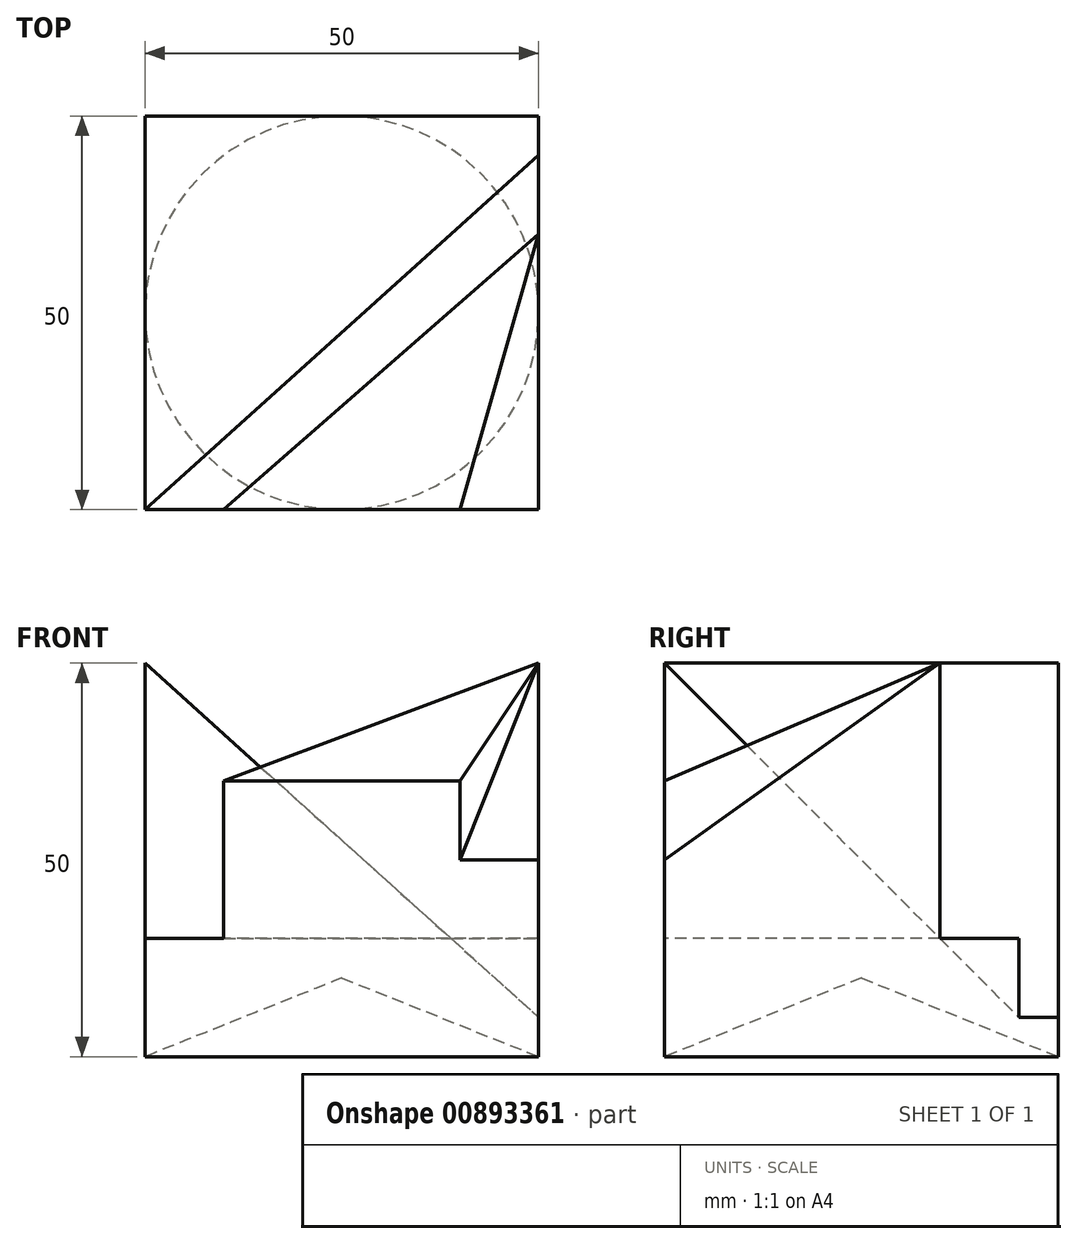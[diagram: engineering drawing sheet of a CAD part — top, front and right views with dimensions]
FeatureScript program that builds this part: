
annotation { "Feature Type Name" : "Feature", "Feature Type Description" : "" }
export const myFeature = defineFeature(function(context is Context, id is Id, definition is map)
    precondition{}
    {
        {
            var Q0;
            Q0=qCreatedBy(makeId("Top.planeOp"),FACE);
            var sketch = newSketch(context, id + "F0", { "sketchPlane" : qUnion([Q0])});
            skLineSegment(sketch, "E0.bottom", {"start": v(25, 25) * mm, "end": v(-25, 25) * mm});
            skLineSegment(sketch, "E0.top", {"start": v(25, -25) * mm, "end": v(-25, -25) * mm});
            skLineSegment(sketch, "E0.left", {"start": v(25, 25) * mm, "end": v(25, -25) * mm});
            skLineSegment(sketch, "E0.right", {"start": v(-25, 25) * mm, "end": v(-25, -25) * mm});
            skPoint(sketch, "E0.middle", {"position": v(0, 0) * mm});
            skSolve(sketch);
        }
        {
            var Q0;
            Q0=makeQuery(id+"F0.imprint","IMPRINT",FACE,{"disambiguationData":[TD([[makeQuery(id+"F0.imprint","IMPRINT",EDGE,{"derivedFrom":sQuery(id+"F0.wireOp",EDGE,"E0.bottom")}),1.0]])]});
            extrude(context, id + "F1", {"entities" : qUnion([Q0]), "depth" : 50 * mm, "offsetDistance" : 25 * mm});
        }
        {
            var Q0;
            Q0=makeQuery(id+"F1.opExtrude","CAP_FACE",FACE,{"disambiguationData":[OSD([sQuery(id+"F0.wireOp",EDGE,"E0.bottom"),sQuery(id+"F0.wireOp",EDGE,"E0.top"),sQuery(id+"F0.wireOp",EDGE,"E0.left"),sQuery(id+"F0.wireOp",EDGE,"E0.right")])],"isStart":true});
            cPlane(context, id + "F2", {"entities" : qUnion([Q0]), "cplaneType" : CPlaneType.OFFSET, "offset" : 15 * mm, "oppositeDirection" : true, "width" : 150 * mm, "height" : 150 * mm});
        }
        {
            var Q0;
            Q0=makeQuery(id+"F1.opExtrude","CAP_FACE",FACE,{"disambiguationData":[OSD([sQuery(id+"F0.wireOp",EDGE,"E0.bottom"),sQuery(id+"F0.wireOp",EDGE,"E0.top"),sQuery(id+"F0.wireOp",EDGE,"E0.left"),sQuery(id+"F0.wireOp",EDGE,"E0.right")])],"isStart":false});
            var sketch = newSketch(context, id + "F3", { "sketchPlane" : qUnion([Q0])});
            skLineSegment(sketch, "E1", {"start": v(-25, -25) * mm, "end": v(25, 20) * mm});
            skLineSegment(sketch, "E2", {"start": v(25, 20) * mm, "end": v(25, 10) * mm});
            skLineSegment(sketch, "E3", {"start": v(25, 10) * mm, "end": v(-15, -25) * mm});
            skLineSegment(sketch, "E4", {"start": v(-15, -25) * mm, "end": v(-25, -25) * mm});
            skSolve(sketch);
        }
        {
            var Q0;
            Q0=makeQuery(id+"F3.imprint","IMPRINT",FACE,{"disambiguationData":[TD([[makeQuery(id+"F3.imprint","IMPRINT",EDGE,{"derivedFrom":sQuery(id+"F3.wireOp",EDGE,"E1")}),-1.0]])]});
            var Q1;
            Q1=qCreatedBy(id+"F2.planeOp",FACE);
            extrude(context, id + "F4", {"entities" : qUnion([Q0]), "operationType" : NewBodyOperationType.REMOVE, "endBound" : BoundingType.UP_TO_SURFACE, "oppositeDirection" : true, "depth" : 25 * mm, "endBoundEntityFace" : qUnion([Q1]), "offsetDistance" : 25 * mm});
        }
        {
            var Q0;
            Q0=qCreatedBy(makeId("Front.planeOp"),FACE);
            var sketch = newSketch(context, id + "F5", { "sketchPlane" : qUnion([Q0])});
            skLineSegment(sketch, "E5", {"start": v(0, 0) * mm, "end": v(0, 10) * mm});
            skLineSegment(sketch, "E6", {"start": v(0, 10) * mm, "end": v(25, 0) * mm});
            skLineSegment(sketch, "E7", {"start": v(25, 0) * mm, "end": v(0, 0) * mm});
            skSolve(sketch);
        }
        {
            var Q0;
            Q0 = qSketchRegion(id + "F5", true);
            var Q1;
            Q1=sQuery(id+"F5.wireOp",EDGE,"E5");
            revolve(context, id + "F6", {"operationType" : NewBodyOperationType.REMOVE, "surfaceOperationType" : NewSurfaceOperationType.NEW, "entities" : qUnion([Q0]), "axis" : qUnion([Q1]), "revolveType" : RevolveType.FULL, "oppositeDirection" : true});
        }
        {
            var Q0;
            Q0=makeQuery(id+"F1.opExtrude","SWEPT_FACE",FACE,{"disambiguationData":[OSD([sQuery(id+"F0.wireOp",EDGE,"E0.top")])]});
            var sketch = newSketch(context, id + "F7", { "sketchPlane" : qUnion([Q0])});
            skLineSegment(sketch, "E8", {"start": v(-15, 50) * mm, "end": v(25, 50) * mm});
            skLineSegment(sketch, "E9", {"start": v(25, 50) * mm, "end": v(25, 25) * mm});
            skLineSegment(sketch, "E10", {"start": v(25, 25) * mm, "end": v(15, 25) * mm});
            skLineSegment(sketch, "E11", {"start": v(15, 25) * mm, "end": v(15, 35) * mm});
            skLineSegment(sketch, "E12", {"start": v(15, 35) * mm, "end": v(-15, 35) * mm});
            skLineSegment(sketch, "E13", {"start": v(-15, 35) * mm, "end": v(-15, 50) * mm});
            skSolve(sketch);
        }
        {
            var Q1;
            Q1=makeQuery(id+"F7.imprint","IMPRINT",FACE,{"disambiguationData":[TD([[makeQuery(id+"F7.imprint","IMPRINT",EDGE,{"derivedFrom":sQuery(id+"F7.wireOp",EDGE,"E8")}),1.0]])]});
            var Q2;
            Q2=makeQuery(id+"F4.boolean.opBoolean","COPY",VERTEX,{"derivedFrom":makeQuery(id+"F4.opExtrude","CAP_VERTEX",VERTEX,{"disambiguationData":[OSD([sQuery(id+"F0.wireOp",EDGE,"E0.left"),sQuery(id+"F3.wireOp",EDGE,"E2"),sQuery(id+"F3.wireOp",EDGE,"E3")])],"isStart":true})});
            loft(context, id + "F8", {"operationType" : NewBodyOperationType.REMOVE, "sheetProfilesArray" : [{ "sheetProfileEntities" : qUnion([Q1]) }, { "sheetProfileEntities" : qUnion([Q2]) }]});
        }
        {
            var Q0;
            Q0=makeQuery(id+"F1.opExtrude","SWEPT_FACE",FACE,{"disambiguationData":[OSD([sQuery(id+"F0.wireOp",EDGE,"E0.bottom")])]});
            var sketch = newSketch(context, id + "F9", { "sketchPlane" : qUnion([Q0])});
            skLineSegment(sketch, "E14", {"start": v(25, 50) * mm, "end": v(-25, 5) * mm});
            skLineSegment(sketch, "E15", {"start": v(-25, 5) * mm, "end": v(-25, 50) * mm});
            skLineSegment(sketch, "E16", {"start": v(-25, 50) * mm, "end": v(25, 50) * mm});
            skSolve(sketch);
        }
        {
            var Q0;
            Q0=makeQuery(id+"F9.imprint","IMPRINT",FACE,{"disambiguationData":[TD([[makeQuery(id+"F9.imprint","IMPRINT",EDGE,{"derivedFrom":sQuery(id+"F9.wireOp",EDGE,"E14")}),-1.0]])]});
            var Q1;
            Q1=makeQuery(id+"F4.boolean.opBoolean","COPY",FACE,{"derivedFrom":makeQuery(id+"F4.opExtrude","SWEPT_FACE",FACE,{"disambiguationData":[OSD([sQuery(id+"F3.wireOp",EDGE,"E1")])]})});
            extrude(context, id + "F10", {"entities" : qUnion([Q0]), "operationType" : NewBodyOperationType.REMOVE, "endBound" : BoundingType.UP_TO_SURFACE, "oppositeDirection" : true, "depth" : 25 * mm, "endBoundEntityFace" : qUnion([Q1]), "offsetDistance" : 25 * mm});
        }
    });
